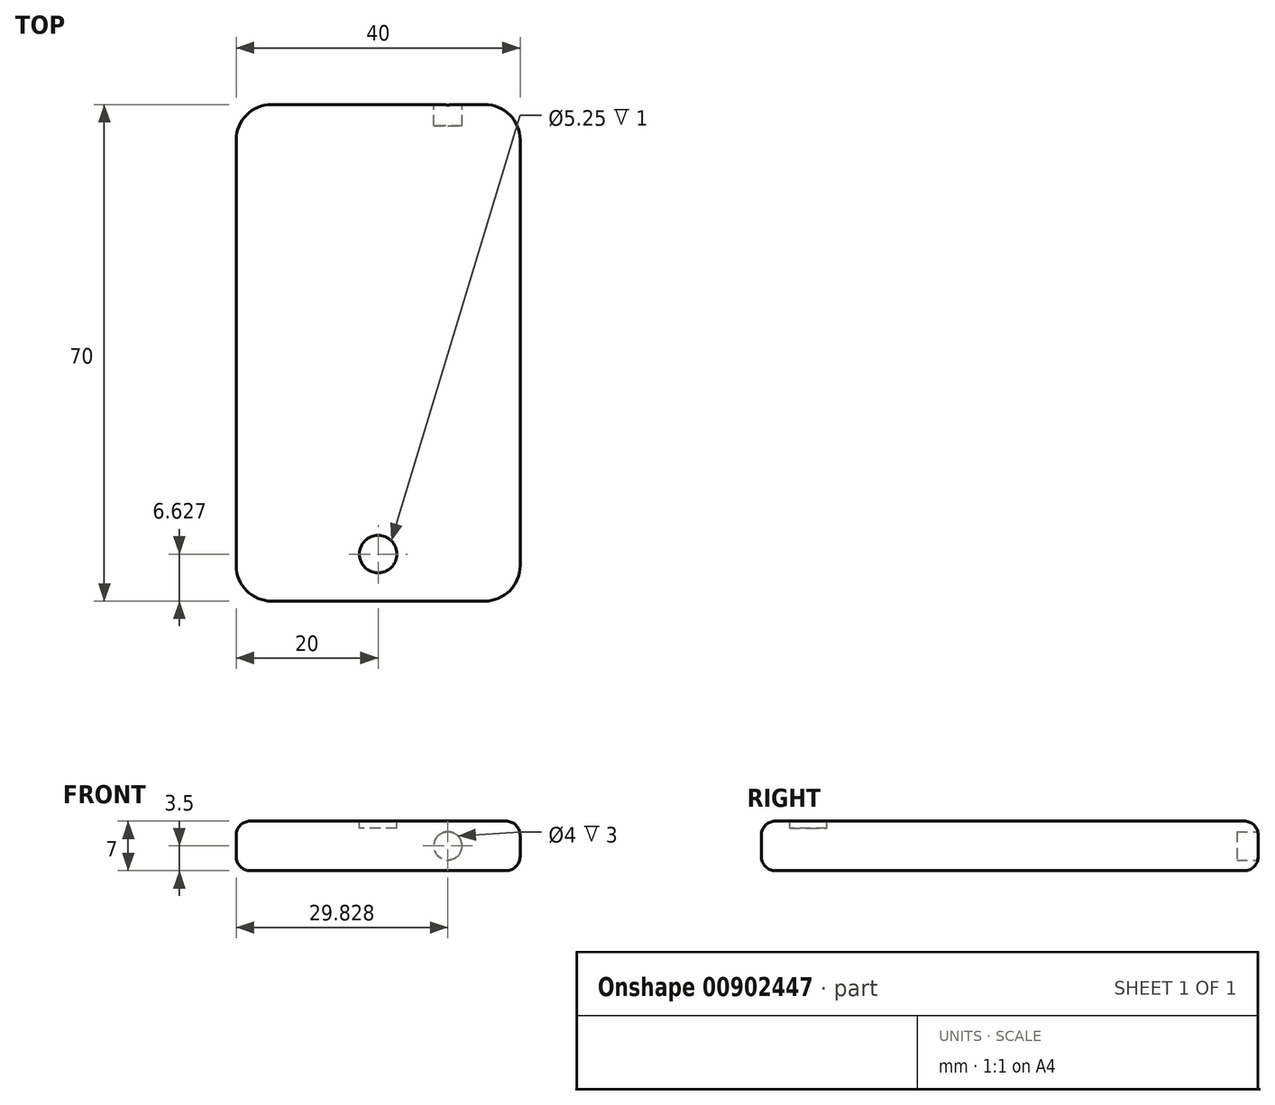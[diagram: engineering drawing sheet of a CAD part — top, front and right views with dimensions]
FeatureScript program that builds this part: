
annotation { "Feature Type Name" : "Feature", "Feature Type Description" : "" }
export const myFeature = defineFeature(function(context is Context, id is Id, definition is map)
    precondition{}
    {
        {
            var Q0;
            Q0=qCreatedBy(makeId("Top.planeOp"),FACE);
            var sketch = newSketch(context, id + "F0", { "sketchPlane" : qUnion([Q0])});
            skLineSegment(sketch, "E0.bottom", {"start": v(0, 0) * mm, "end": v(40, 0) * mm});
            skLineSegment(sketch, "E0.top", {"start": v(0, 70) * mm, "end": v(40, 70) * mm});
            skLineSegment(sketch, "E0.left", {"start": v(0, 0) * mm, "end": v(0, 70) * mm});
            skLineSegment(sketch, "E0.right", {"start": v(40, 0) * mm, "end": v(40, 70) * mm});
            skSolve(sketch);
        }
        {
            var Q0;
            Q0 = qSketchRegion(id + "F0", true);
            extrude(context, id + "F1", {"entities" : qUnion([Q0]), "depth" : 7 * mm, "offsetDistance" : 25 * mm});
        }
        {
            var Q0;
            Q0=makeQuery(id+"F1.opExtrude","SWEPT_EDGE",EDGE,{"disambiguationData":[OSD([sQuery(id+"F0.wireOp",EDGE,"E0.top"),sQuery(id+"F0.wireOp",EDGE,"E0.right")])]});
            var Q1;
            Q1=makeQuery(id+"F1.opExtrude","SWEPT_EDGE",EDGE,{"disambiguationData":[OSD([sQuery(id+"F0.wireOp",EDGE,"E0.top"),sQuery(id+"F0.wireOp",EDGE,"E0.left")])]});
            var Q2;
            Q2=makeQuery(id+"F1.opExtrude","SWEPT_EDGE",EDGE,{"disambiguationData":[OSD([sQuery(id+"F0.wireOp",EDGE,"E0.bottom"),sQuery(id+"F0.wireOp",EDGE,"E0.right")])]});
            var Q3;
            Q3=makeQuery(id+"F1.opExtrude","SWEPT_EDGE",EDGE,{"disambiguationData":[OSD([sQuery(id+"F0.wireOp",EDGE,"E0.bottom"),sQuery(id+"F0.wireOp",EDGE,"E0.left")])]});
            fillet(context, id + "F2", {"entities" : qUnion([Q0, Q1, Q2, Q3]), "radius" : 5 * mm, "tangentPropagation" : true, "allowEdgeOverflow" : false});
        }
        {
            var Q0;
            Q0=makeQuery(id+"F1.opExtrude","SWEPT_FACE",FACE,{"disambiguationData":[OSD([sQuery(id+"F0.wireOp",EDGE,"E0.top")])]});
            var sketch = newSketch(context, id + "F3", { "sketchPlane" : qUnion([Q0])});
            skCircle(sketch, "E1", {"center": v(-29.83, 3.5) * mm, "radius": 2 * mm});
            skPoint(sketch, "E1.centerSnap0", {"position": v(-35, 3.5) * mm});
            skSolve(sketch);
        }
        {
            var Q0;
            Q0 = qSketchRegion(id + "F3", true);
            extrude(context, id + "F4", {"entities" : qUnion([Q0]), "operationType" : NewBodyOperationType.REMOVE, "oppositeDirection" : true, "depth" : 3 * mm, "offsetDistance" : 25 * mm});
        }
        {
            var Q0;
            Q0=makeQuery(id+"F1.opExtrude","CAP_EDGE",EDGE,{"disambiguationData":[OSD([sQuery(id+"F0.wireOp",EDGE,"E0.left")])],"isStart":false});
            var Q1;
            Q1=makeQuery(id+"F1.opExtrude","CAP_EDGE",EDGE,{"disambiguationData":[OSD([sQuery(id+"F0.wireOp",EDGE,"E0.left")])],"isStart":true});
            fillet(context, id + "F5", {"entities" : qUnion([Q0, Q1]), "radius" : 2 * mm, "tangentPropagation" : true, "allowEdgeOverflow" : false});
        }
        {
            var Q0;
            Q0=makeQuery(id+"F1.opExtrude","CAP_FACE",FACE,{"disambiguationData":[OSD([sQuery(id+"F0.wireOp",EDGE,"E0.bottom"),sQuery(id+"F0.wireOp",EDGE,"E0.top"),sQuery(id+"F0.wireOp",EDGE,"E0.left"),sQuery(id+"F0.wireOp",EDGE,"E0.right")])],"isStart":false});
            var sketch = newSketch(context, id + "F6", { "sketchPlane" : qUnion([Q0])});
            skCircle(sketch, "E2", {"center": v(20, 6.63) * mm, "radius": 2.63 * mm});
            skPoint(sketch, "E2.centerSnap0", {"position": v(20, 2) * mm});
            skSolve(sketch);
        }
        {
            var Q0;
            Q0=makeQuery(id+"F6.imprint","IMPRINT",FACE,{"disambiguationData":[TD([[makeQuery(id+"F6.imprint","IMPRINT",EDGE,{"derivedFrom":sQuery(id+"F6.wireOp",EDGE,"E2")}),1.0]])]});
            extrude(context, id + "F7", {"entities" : qUnion([Q0]), "operationType" : NewBodyOperationType.REMOVE, "oppositeDirection" : true, "depth" : 1 * mm, "offsetDistance" : 25 * mm});
        }
    });
